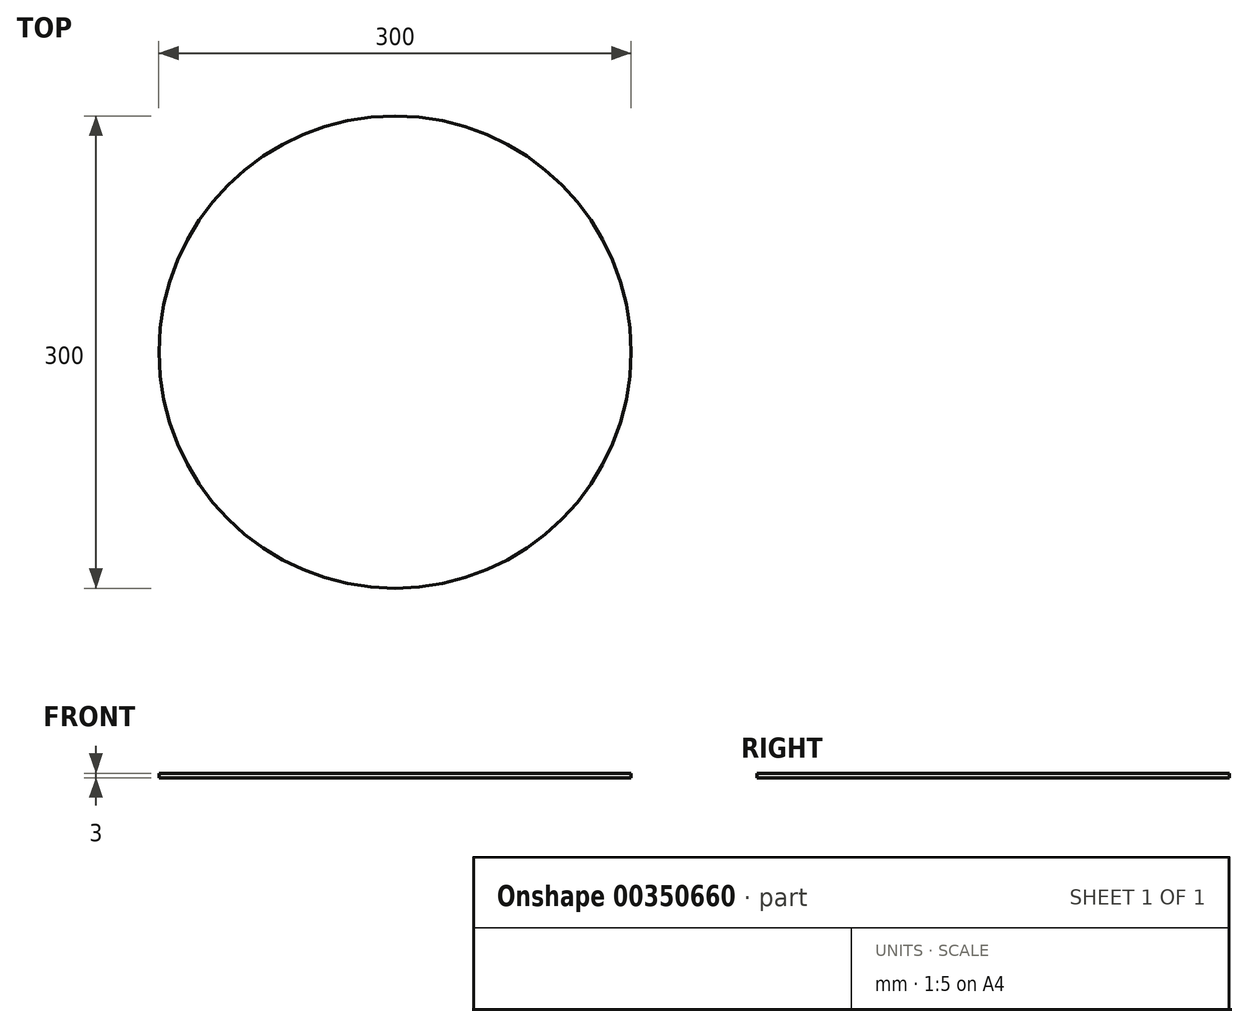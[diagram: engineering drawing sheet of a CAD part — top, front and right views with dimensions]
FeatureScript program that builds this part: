
annotation { "Feature Type Name" : "Feature", "Feature Type Description" : "" }
export const myFeature = defineFeature(function(context is Context, id is Id, definition is map)
    precondition{}
    {
        {
            var Q0;
            Q0=qCreatedBy(makeId("Top.planeOp"),FACE);
            var sketch = newSketch(context, id + "F0", { "sketchPlane" : qUnion([Q0])});
            skCircle(sketch, "E0", {"center": v(-442.49, 24.21) * mm, "radius": 150 * mm});
            skSolve(sketch);
        }
        {
            var Q0;
            Q0=qSketchRegion(id+"F0",true);
            extrude(context, id + "F1", {"entities" : qUnion([Q0]), "depth" : 3 * mm});
        }
    });
